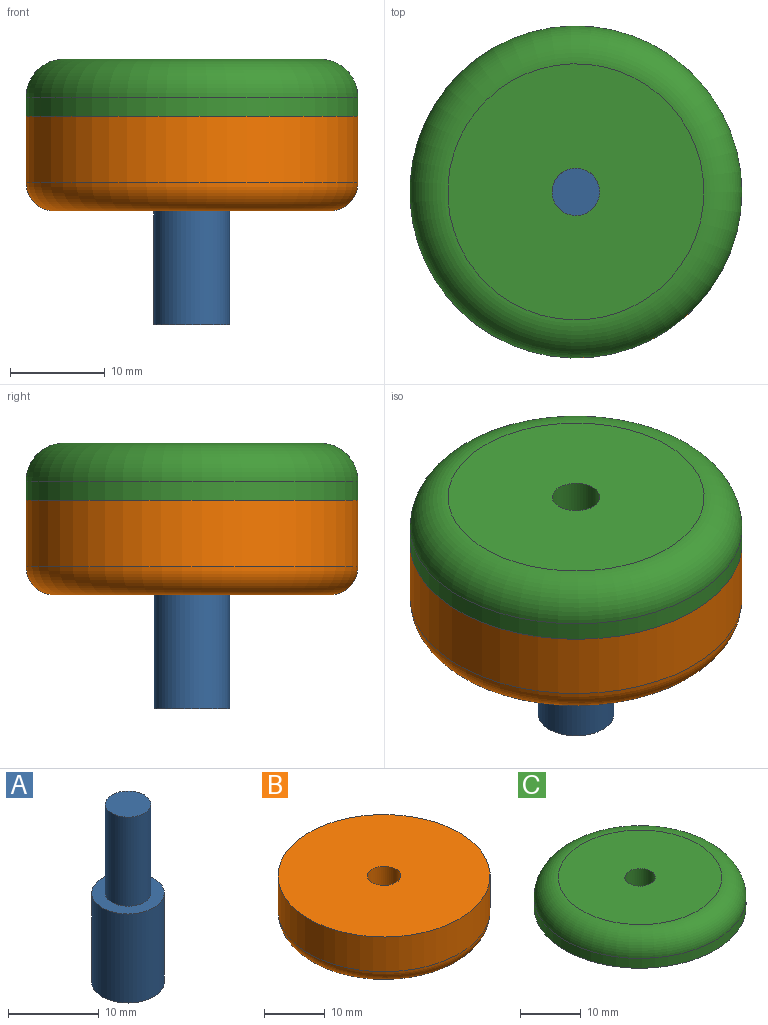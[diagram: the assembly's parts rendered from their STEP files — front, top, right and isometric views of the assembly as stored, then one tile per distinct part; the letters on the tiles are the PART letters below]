
ASSEMBLY  parts=3 mates=3
PART A: 5 faces, bbox 8x8x24 mm
  f0: cylinder r=4mm len=12mm, axis (0,0,-1), area 301.6mm2, adj f1,f2
  f1: plane 8x8mm, normal (0,0,1), area 30.6mm2, adj f0,f3
  f2: plane 8x8mm, normal (0,0,-1), area 50.3mm2, adj f0
  f3: cylinder r=2.5mm len=12mm, axis (0,0,-1), area 188.5mm2, adj f1,f4
  f4: plane 5x5mm, normal (0,0,1), area 19.6mm2, adj f3
PART B: 5 faces, bbox 37.9x37.9x10 mm
  f0: cylinder r=2.75mm len=10mm, axis (0,0,-1), area 172.8mm2, adj f2,f3
  f1: cylinder r=17.5mm len=35mm, axis (0,0,-1), area 769.7mm2, adj f2,f4
  f2: plane 35x35mm, normal (0,0,1), area 938.4mm2, adj f0,f1
  f3: plane 29x29mm, normal (0,0,-1), area 636.8mm2, adj f0,f4
  f4: torus R=14.5mm, axis (0,0,1), area 485.9mm2, adj f1,f3
PART C: 5 faces, bbox 37.9x37.9x6 mm
  f0: cylinder r=2.5mm len=6mm, axis (0,0,-1), area 94.2mm2, adj f2,f3
  f1: cylinder r=17.5mm len=35mm, axis (0,0,-1), area 219.9mm2, adj f3,f4
  f2: plane 27x27mm, normal (0,0,1), area 552.9mm2, adj f0,f4
  f3: plane 35x35mm, normal (0,0,-1), area 942.5mm2, adj f0,f1
  f4: torus R=13.5mm, axis (0,0,1), area 633.5mm2, adj f1,f2
PLACE A t=(-2.15,10.27,-2.81)mm
PLACE B t=(-2.15,10.27,9.19)mm
PLACE C t=(-2.15,10.27,19.19)mm
MATE cylindrical C.f0 <-> A.f3  axis (0,0,-1) through (-2.15,10.27,25.19)mm
MATE fastened B.f1 <-> A.f0  axis (0,0,-1) through (-2.15,10.27,9.19)mm
MATE planar C.f1 <-> B.f1  axis (0,0,-1) through (-2.15,10.27,19.19)mm
